MODEL slx_01a87a64ffad
CONFIG AbsTol = auto
CONFIG EnableMultiTasking = off
CONFIG FixedStep = auto
CONFIG MaxStep = auto
CONFIG MinStep = auto
CONFIG RelTol = 1e-3
CONFIG SampleTimeConstraint = Unconstrained
CONFIG SolverName = VariableStepAuto
CONFIG StartTime = 0.0
CONFIG StopTime = 0.3
BLOCK [CCaller] C Caller
  FunctionName = Sguan_Loop
  PortSpecificationStruct = %)30     .    8 4   8    (     @         %    "     ,    !     0         %  0 "0    $    _    07)G3F%M90  4&]R=$YA;64 4V-O<&4     26YD97@     5'EP90      4VEZ90      27-';&]B86P   X    P    !@    @    $          4    (     0    ,    !         !   P!R968 #@   #     &    "     0         !0    @    !     P    $         $  # ')E9@ .    .     8    (    !          %    "     $    %     0         0    !0...<+1448ch>
  SampleTime = 0.0005
BLOCK [Reference] Iq1  REF=powerlib_extras/Discrete 
Control Blocks/Discrete
PI Controller
  NameLocation = top
  SourceBlock = powerlib_extras/Discrete 
Control Blocks/Discrete
PI Controller
  SourceType = Discrete PI Controller
BLOCK [ZeroOrderHold] Ladrc调控信号(闭环250rad//s)
  NameLocation = top
  SampleTime = 0.0005
BLOCK [Sum] PI零极点对消调控信号(闭环250rad//s)
  Inputs = ++|
BLOCK [Scope] Scope10
  ActiveDisplayYMaximum = 664.214721107104
  ActiveDisplayYMinimum = -226.95199850252726
  DataLoggingVariableName = ScopeData10
  Floating = off
  GraphicalSettings = {"Style":{"BackgroundColor":[0.12941176470588237,0.12941176470588237,0.12941176470588237],"AxesColor":[0.07058823529411765,0.07058823529411765,0.07058823529411765],"LabelsColor":[0.8509803921568627,0.8509803921568627,0.8509803921568627],"PreserveColors":false,"Visible":[true],"LineStyle":["-"],"LineWidth":[1.5],"BarWidth":[0.9],"LineColor":["auto"],"LineFaceAlpha":[1],"LineEdgeAlpha":[1],"Marker":...<+1987ch>
  MultipleDisplayCache = [{"MaxYLimMag":527.88712692260742,"MaxYLimReal":664.214721107104,"MinYLimMag":0,"MinYLimReal":-226.95199850252726,"PlotAsMagnitudePhase":false,"ShowGrid":true,"ShowLegend":false,"Title":"%<SignalLabel>","YLabel":""}]
  NumInputPorts = 1
  ScopeFrameLocation = window
  WasSavedAsWebScope = on
  WindowPosition = [573.000000,323.000000,560.000000,420.000000,]
BLOCK [Sum] Sum4
  Inputs = |+-
  NameLocation = left
BLOCK [Sum] Sum5
  Inputs = ++|
BLOCK [ZeroOrderHold] Zero-Order Hold1
  SampleTime = 0.0005
BLOCK [TransferFcn] fun
  Denominator = [1 0.3*350 122500]
  Numerator = [122500]
BLOCK [TransferFcn] fun1
  Denominator = [1 0.3*350 122500]
  Numerator = [122500]
BLOCK [TransferFcn] fun2
  Denominator = [1 0.3*350 122500]
  Numerator = [122500]
BLOCK [Step] set2
  After = 500
  NameLocation = top
  SampleTime = 0
  Time = 0.05
BLOCK [Step] 干扰
  After = -50
  Before = -20
  NameLocation = top
  SampleTime = 0
  Time = 0.2
BLOCK [Step] 干扰1
  After = -50
  Before = -20
  NameLocation = top
  SampleTime = 0
  Time = 0.2
BLOCK [Scope] 控制器示波器
  ActiveDisplayYMaximum = 901.74005280672577
  ActiveDisplayYMinimum = -111.30445031185839
  DataLoggingVariableName = ScopeData9
  Floating = off
  GraphicalSettings = {"Style":{"BackgroundColor":[0.9411764705882353,0.9411764705882353,0.9411764705882353],"AxesColor":[1,1,1],"LabelsColor":[0.6509803921568628,0.6509803921568628,0.6509803921568628],"PreserveColors":false,"Visible":[true,true,true,true],"LineStyle":["-","-","-","-"],"LineWidth":[1.5,1.5,1.5,1.5],"BarWidth":[0.9,0.9,0.9,0.9],"LineColor":["auto","auto","auto","auto"],"LineFaceAlpha":[1,1,1,1],"LineEdg...<+2355ch>
  LayoutDimensionsString = [1,1]
  MultipleDisplayCache = [{"MaxYLimMag":562.5,"MaxYLimReal":901.74005280672577,"MinYLimMag":0,"MinYLimReal":-111.30445031185839,"PlotAsMagnitudePhase":false,"ShowGrid":true,"ShowLegend":true,"Title":"%<SignalLabel>","YLabel":""}]
  NumInputPorts = 4
  ScopeFrameLocation = window
  ShowLegend = on
  WasSavedAsWebScope = on
  WindowPosition = [330.000000,351.000000,857.000000,567.000000,]
BLOCK [Sum] 无调优的信号(开环350rad//s)
  Inputs = |++
BLOCK [Step] 输入期望Signal（阶跃）
  After = 500
  NameLocation = top
  SampleTime = 0
  Time = 0.05
LINE C Caller:1 -> Scope10:1
LINE C Caller:1 -> fun:1
LINE Iq1:1 -> fun1:1
LINE Ladrc调控信号(闭环250rad//s):1 -> C Caller:2
LINE Ladrc调控信号(闭环250rad//s):1 -> 控制器示波器:4
LINE PI零极点对消调控信号(闭环250rad//s):1 -> Sum4:2
LINE PI零极点对消调控信号(闭环250rad//s):1 -> 控制器示波器:3
LINE Sum4:1 -> Iq1:1
LINE Sum5:1 -> Ladrc调控信号(闭环250rad//s):1
LINE Zero-Order Hold1:1 -> C Caller:1
LINE fun1:1 -> PI零极点对消调控信号(闭环250rad//s):1
LINE fun2:1 -> 无调优的信号(开环350rad//s):2
LINE fun:1 -> Sum5:2
LINE set2:1 -> fun2:1
LINE 干扰1:1 -> PI零极点对消调控信号(闭环250rad//s):2
LINE 干扰1:1 -> 无调优的信号(开环350rad//s):1
LINE 干扰:1 -> Sum5:1
LINE 无调优的信号(开环350rad//s):1 -> 控制器示波器:2
LINE 输入期望Signal（阶跃）:1 -> Sum4:1
LINE 输入期望Signal（阶跃）:1 -> Zero-Order Hold1:1
LINE 输入期望Signal（阶跃）:1 -> 控制器示波器:1
